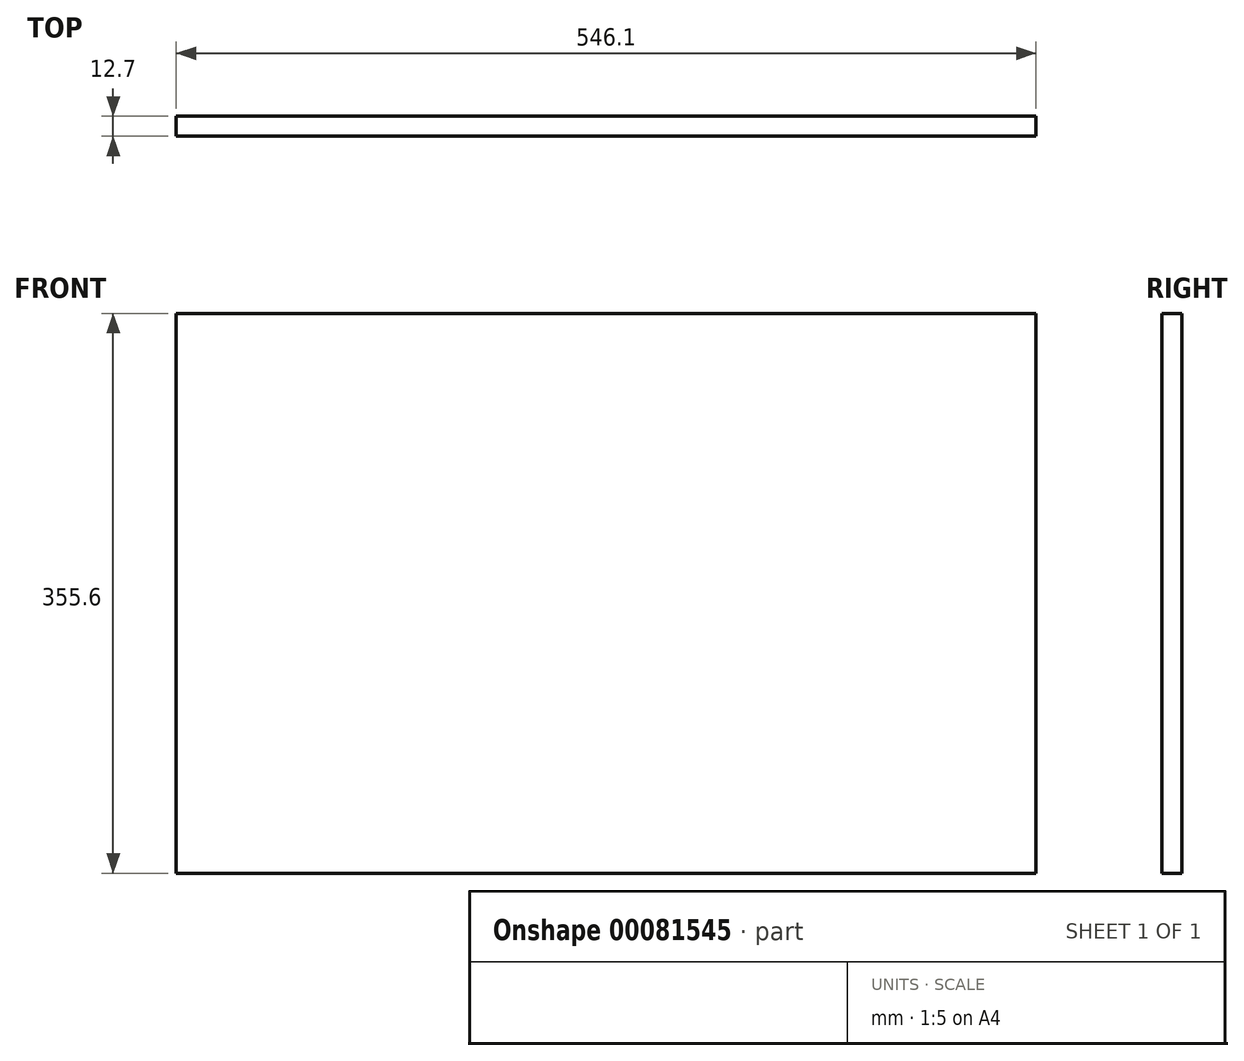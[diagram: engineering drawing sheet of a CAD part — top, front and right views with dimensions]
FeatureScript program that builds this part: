
annotation { "Feature Type Name" : "Feature", "Feature Type Description" : "" }
export const myFeature = defineFeature(function(context is Context, id is Id, definition is map)
    precondition{}
    {
        {
            var Q0;
            Q0=qCreatedBy(makeId("Front.planeOp"),FACE);
            var sketch = newSketch(context, id + "F0", { "sketchPlane" : qUnion([Q0])});
            skLineSegment(sketch, "E0.bottom", {"start": v(273.05, 177.8) * mm, "end": v(-273.05, 177.8) * mm});
            skLineSegment(sketch, "E0.top", {"start": v(273.05, -177.8) * mm, "end": v(-273.05, -177.8) * mm});
            skLineSegment(sketch, "E0.left", {"start": v(273.05, 177.8) * mm, "end": v(273.05, -177.8) * mm});
            skLineSegment(sketch, "E0.right", {"start": v(-273.05, 177.8) * mm, "end": v(-273.05, -177.8) * mm});
            skPoint(sketch, "E0.middle", {"position": v(0, 0) * mm});
            skSolve(sketch);
        }
        {
            var Q0;
            Q0 = qSketchRegion(id + "F0", true);
            extrude(context, id + "F1", {"entities" : qUnion([Q0]), "depth" : 12.7 * mm});
        }
    });
